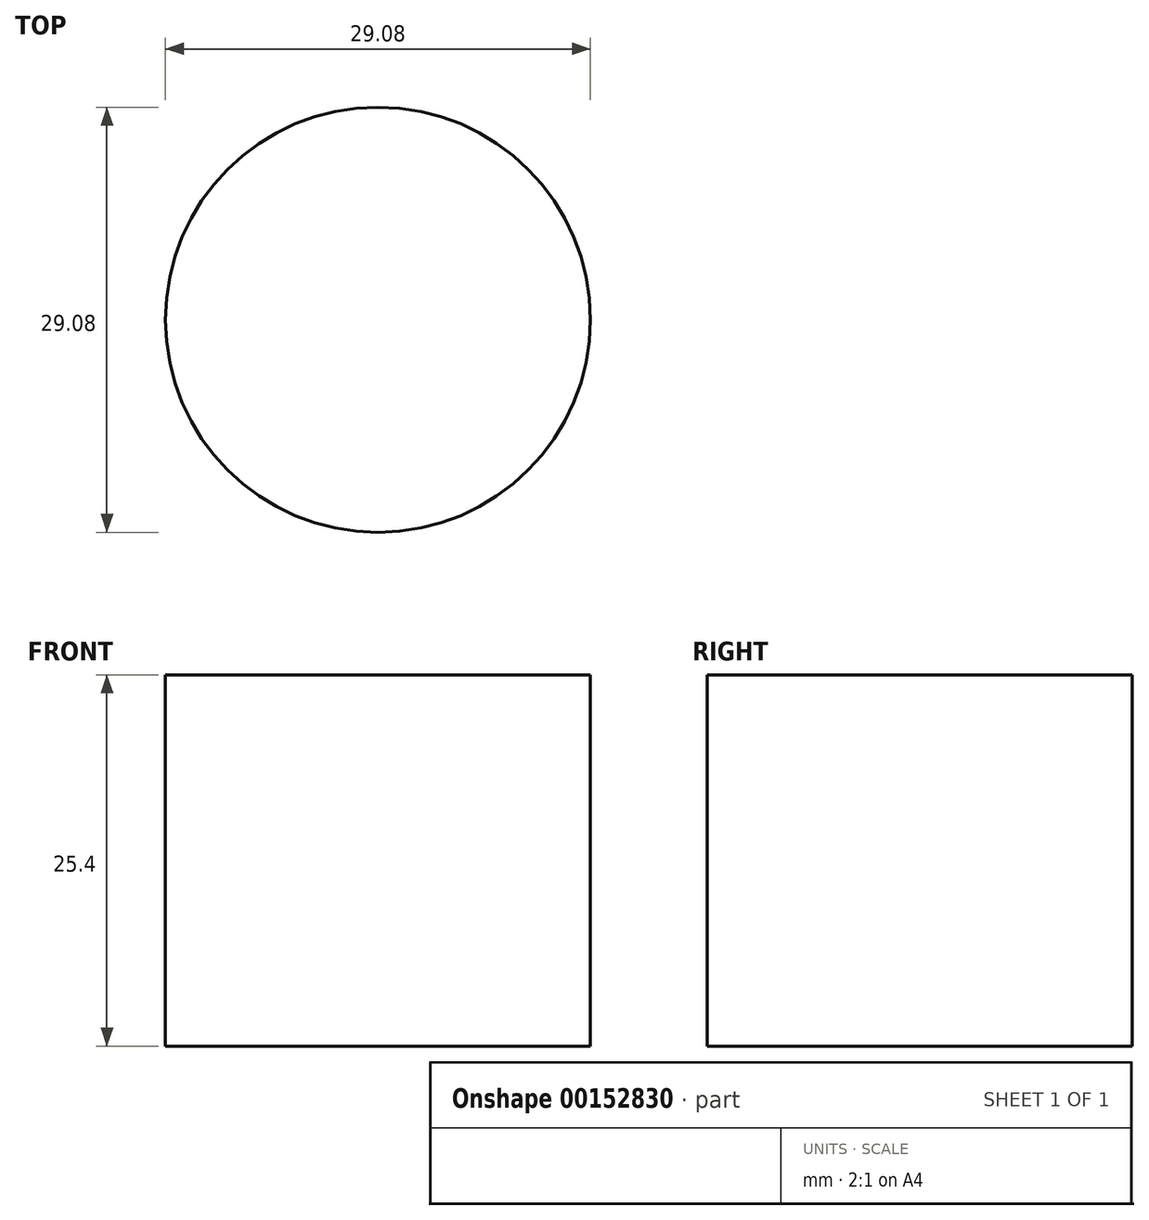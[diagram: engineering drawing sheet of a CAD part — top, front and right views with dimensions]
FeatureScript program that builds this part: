
annotation { "Feature Type Name" : "Feature", "Feature Type Description" : "" }
export const myFeature = defineFeature(function(context is Context, id is Id, definition is map)
    precondition{}
    {
        {
            var Q0;
            Q0=qCreatedBy(makeId("Top.planeOp"),FACE);
            var sketch = newSketch(context, id + "F0", { "sketchPlane" : qUnion([Q0])});
            skCircle(sketch, "E0", {"center": v(0, 0) * mm, "radius": 14.54 * mm});
            skSolve(sketch);
        }
        {
            var Q0;
            Q0 = qSketchRegion(id + "F0", true);
            extrude(context, id + "F1", {"entities" : qUnion([Q0]), "depth" : 25.4 * mm});
        }
    });
